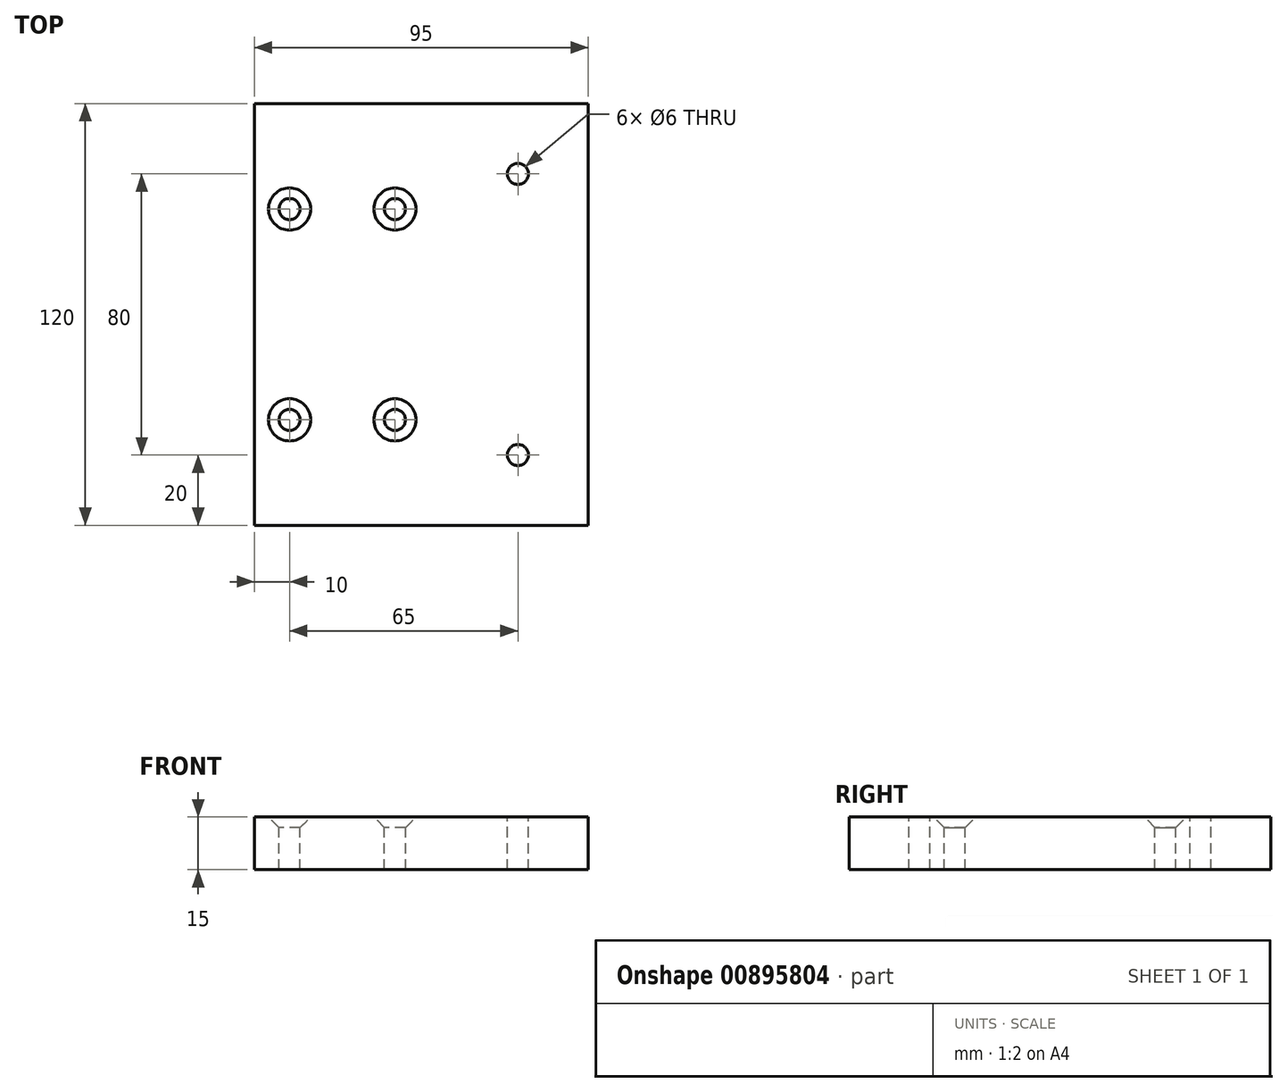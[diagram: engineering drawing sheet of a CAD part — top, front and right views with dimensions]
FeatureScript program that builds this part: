
annotation { "Feature Type Name" : "Feature", "Feature Type Description" : "" }
export const myFeature = defineFeature(function(context is Context, id is Id, definition is map)
    precondition{}
    {
        {
            var Q0;
            Q0=qCreatedBy(makeId("Top.planeOp"),FACE);
            var sketch = newSketch(context, id + "F0", { "sketchPlane" : qUnion([Q0])});
            skLineSegment(sketch, "E0.bottom", {"start": v(-47.5, 60) * mm, "end": v(47.5, 60) * mm});
            skLineSegment(sketch, "E0.top", {"start": v(-47.5, -60) * mm, "end": v(47.5, -60) * mm});
            skLineSegment(sketch, "E0.left", {"start": v(-47.5, 60) * mm, "end": v(-47.5, -60) * mm});
            skLineSegment(sketch, "E0.right", {"start": v(47.5, 60) * mm, "end": v(47.5, -60) * mm});
            skPoint(sketch, "E0.middle", {"position": v(0, 0) * mm});
            skCircle(sketch, "E1", {"center": v(-37.5, 30) * mm, "radius": 3 * mm});
            skCircle(sketch, "E2", {"center": v(-7.5, 30) * mm, "radius": 3 * mm});
            skCircle(sketch, "E3.MirrorC", {"center": v(-7.5, -30) * mm, "radius": 3 * mm});
            skCircle(sketch, "E4.MirrorC", {"center": v(-37.5, -30) * mm, "radius": 3 * mm});
            skCircle(sketch, "E5", {"center": v(27.5, 40) * mm, "radius": 3 * mm});
            skCircle(sketch, "E6.MirrorC", {"center": v(27.5, -40) * mm, "radius": 3 * mm});
            skSolve(sketch);
        }
        {
            var Q0;
            Q0=qSketchRegion(id+"F0",true);
            var Q1;
            Q1=makeQuery(id+"F0.imprint","IMPRINT",FACE,{"disambiguationData":[TD([[makeQuery(id+"F0.imprint","IMPRINT",EDGE,{"derivedFrom":sQuery(id+"F0.wireOp",EDGE,"E1")}),1.0]])]});
            var Q2;
            Q2=makeQuery(id+"F0.imprint","IMPRINT",FACE,{"disambiguationData":[TD([[makeQuery(id+"F0.imprint","IMPRINT",EDGE,{"derivedFrom":sQuery(id+"F0.wireOp",EDGE,"E4.MirrorC")}),-1.0]])]});
            var Q3;
            Q3=makeQuery(id+"F0.imprint","IMPRINT",FACE,{"disambiguationData":[TD([[makeQuery(id+"F0.imprint","IMPRINT",EDGE,{"derivedFrom":sQuery(id+"F0.wireOp",EDGE,"E3.MirrorC")}),-1.0]])]});
            var Q4;
            Q4=makeQuery(id+"F0.imprint","IMPRINT",FACE,{"disambiguationData":[TD([[makeQuery(id+"F0.imprint","IMPRINT",EDGE,{"derivedFrom":sQuery(id+"F0.wireOp",EDGE,"E6.MirrorC")}),-1.0]])]});
            var Q5;
            Q5=makeQuery(id+"F0.imprint","IMPRINT",FACE,{"disambiguationData":[TD([[makeQuery(id+"F0.imprint","IMPRINT",EDGE,{"derivedFrom":sQuery(id+"F0.wireOp",EDGE,"E2")}),1.0]])]});
            var Q6;
            Q6=makeQuery(id+"F0.imprint","IMPRINT",FACE,{"disambiguationData":[TD([[makeQuery(id+"F0.imprint","IMPRINT",EDGE,{"derivedFrom":sQuery(id+"F0.wireOp",EDGE,"E5")}),1.0]])]});
            extrude(context, id + "F1", {"entities" : qUnion([Q0, Q1, Q2, Q3, Q4, Q5, Q6]), "oppositeDirection" : true, "depth" : 15 * mm});
        }
        {
            var Q0;
            Q0=sQuery(id+"F0.wireOp",VERTEX,"E1.center");
            var Q1;
            Q1=sQuery(id+"F0.wireOp",VERTEX,"E2.center");
            var Q2;
            Q2=sQuery(id+"F0.wireOp",VERTEX,"E4.MirrorC.center");
            var Q3;
            Q3=sQuery(id+"F0.wireOp",VERTEX,"E3.MirrorC.center");
            var Q4;
            Q4=makeQuery(id+"F1.opExtrude","SWEPT_BODY",BODY,{"disambiguationData":[OSD([sQuery(id+"F0.wireOp",EDGE,"E0.bottom"),sQuery(id+"F0.wireOp",EDGE,"E0.top"),sQuery(id+"F0.wireOp",EDGE,"E0.left"),sQuery(id+"F0.wireOp",EDGE,"E0.right")])]});
            hole(context, id + "F2", {"style" : HoleStyle.C_SINK, "endStyle" : HoleEndStyle.THROUGH, "holeDiameter" : 6 * mm, "cSinkDiameter" : 12 * mm, "cSinkAngle" : 90 * degree, "locations" : qUnion([Q0, Q1, Q2, Q3]), "scope" : qUnion([Q4]), "isTappedThrough" : true});
        }
        {
            var Q0;
            Q0=sQuery(id+"F0.wireOp",VERTEX,"E5.center");
            var Q1;
            Q1=sQuery(id+"F0.wireOp",VERTEX,"E6.MirrorC.center");
            var Q2;
            Q2=makeQuery(id+"F1.opExtrude","SWEPT_BODY",BODY,{"disambiguationData":[OSD([sQuery(id+"F0.wireOp",EDGE,"E0.bottom"),sQuery(id+"F0.wireOp",EDGE,"E0.top"),sQuery(id+"F0.wireOp",EDGE,"E0.left"),sQuery(id+"F0.wireOp",EDGE,"E0.right")])]});
            hole(context, id + "F3", {"style" : HoleStyle.SIMPLE, "endStyle" : HoleEndStyle.THROUGH, "holeDiameter" : 6 * mm, "locations" : qUnion([Q0, Q1]), "scope" : qUnion([Q2]), "isTappedThrough" : true});
        }
    });
